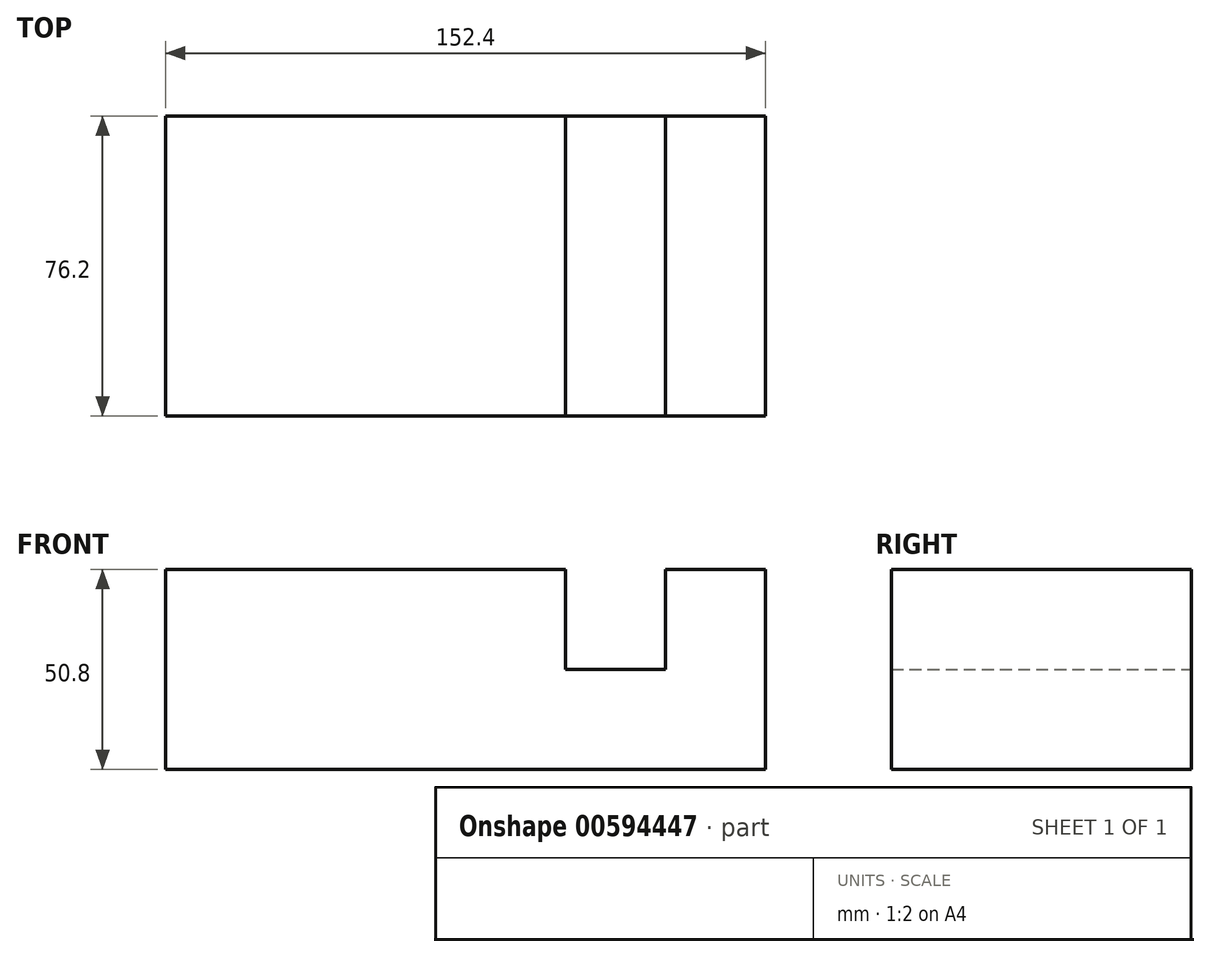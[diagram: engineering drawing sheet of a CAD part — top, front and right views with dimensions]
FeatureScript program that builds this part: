
annotation { "Feature Type Name" : "Feature", "Feature Type Description" : "" }
export const myFeature = defineFeature(function(context is Context, id is Id, definition is map)
    precondition{}
    {
        {
            var Q0;
            Q0=qCreatedBy(makeId("Front.planeOp"),FACE);
            var sketch = newSketch(context, id + "F0", { "sketchPlane" : qUnion([Q0])});
            skLineSegment(sketch, "E0", {"start": v(0, 0) * mm, "end": v(0, 50.8) * mm});
            skLineSegment(sketch, "E1", {"start": v(0, 50.8) * mm, "end": v(101.6, 50.8) * mm});
            skLineSegment(sketch, "E2", {"start": v(101.6, 50.8) * mm, "end": v(101.6, 25.4) * mm});
            skLineSegment(sketch, "E3", {"start": v(101.6, 25.4) * mm, "end": v(127, 25.4) * mm});
            skLineSegment(sketch, "E4", {"start": v(127, 25.4) * mm, "end": v(127, 50.8) * mm});
            skLineSegment(sketch, "E5", {"start": v(127, 50.8) * mm, "end": v(152.4, 50.8) * mm});
            skLineSegment(sketch, "E6", {"start": v(152.4, 50.8) * mm, "end": v(152.4, 0) * mm});
            skLineSegment(sketch, "E7", {"start": v(152.4, 0) * mm, "end": v(0, 0) * mm});
            skSolve(sketch);
        }
        {
            var Q0;
            Q0=makeQuery(id+"F0.imprint","IMPRINT",FACE,{"disambiguationData":[TD([[makeQuery(id+"F0.imprint","IMPRINT",EDGE,{"derivedFrom":sQuery(id+"F0.wireOp",EDGE,"E0")}),-1.0]])]});
            extrude(context, id + "F1", {"entities" : qUnion([Q0]), "depth" : 76.2 * mm, "offsetDistance" : 25.4 * mm});
        }
    });
